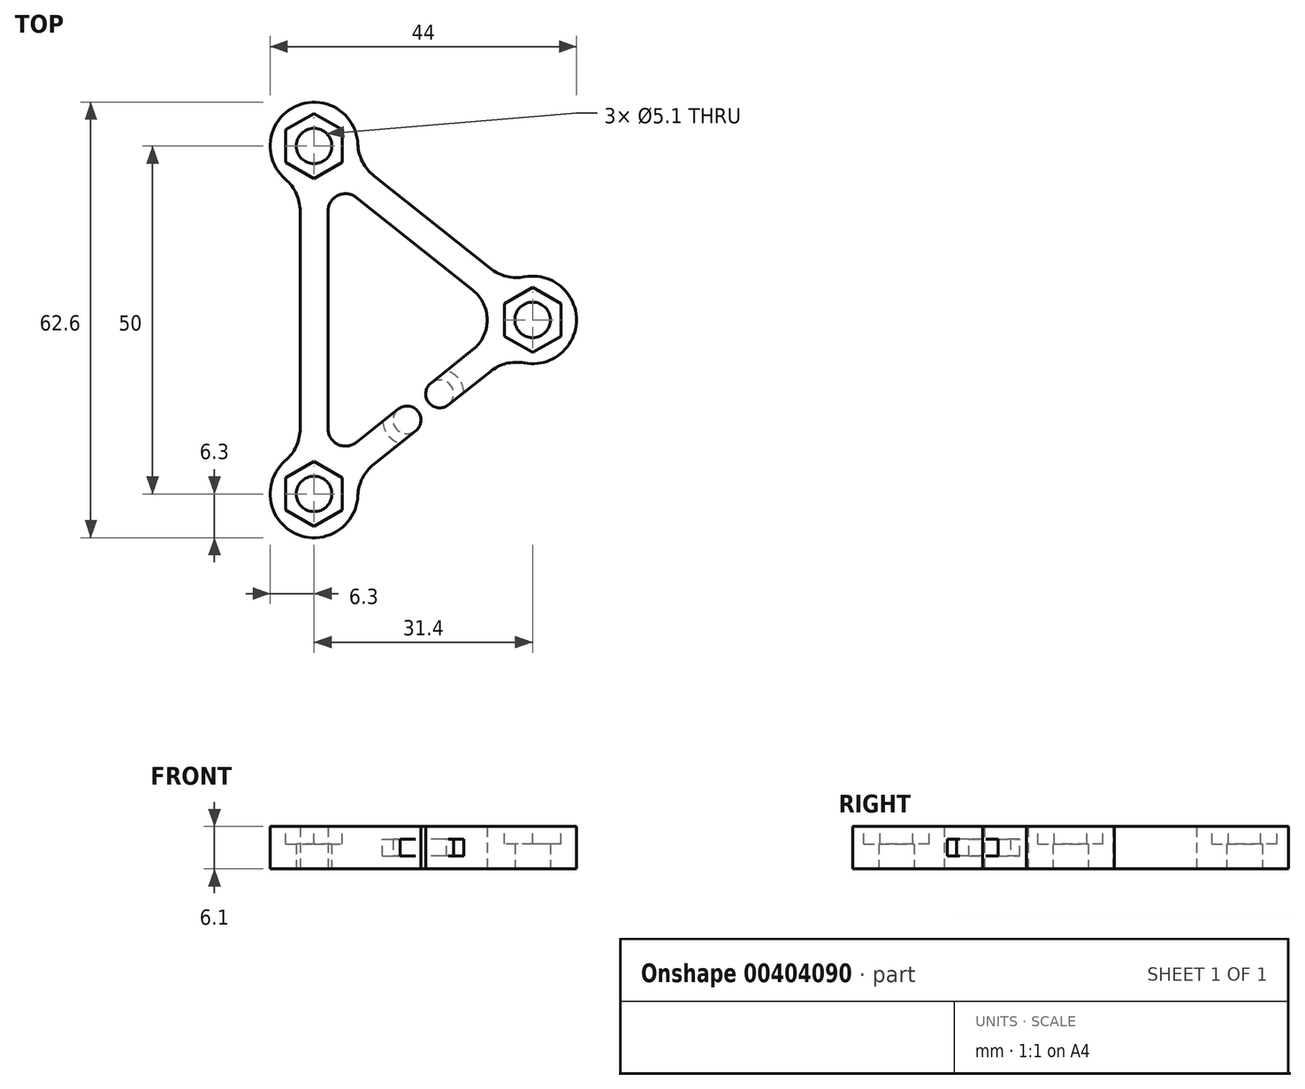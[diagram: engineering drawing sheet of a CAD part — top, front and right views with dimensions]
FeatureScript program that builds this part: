
annotation { "Feature Type Name" : "Feature", "Feature Type Description" : "" }
export const myFeature = defineFeature(function(context is Context, id is Id, definition is map)
    precondition{}
    {
        {
            var Q0;
            Q0=qCreatedBy(makeId("Top.planeOp"),FACE);
            var sketch = newSketch(context, id + "F0", { "sketchPlane" : qUnion([Q0])});
            skCircle(sketch, "E0", {"center": v(-31.4, 25) * mm, "radius": 2.55 * mm});
            skCircle(sketch, "E1", {"center": v(-31.4, -25) * mm, "radius": 2.55 * mm});
            skCircle(sketch, "E2", {"center": v(0, 0) * mm, "radius": 2.55 * mm});
            skArc(sketch, "E3", {"start": v(-25.1, 25.25) * mm, "mid": v(-34.14, 30.68) * mm, "end": v(-35.52, 20.23) * mm});
            skArc(sketch, "E4", {"start": v(-35.52, -20.23) * mm, "mid": v(-34.14, -30.68) * mm, "end": v(-25.1, -25.25) * mm});
            skArc(sketch, "E5", {"start": v(-1.17, -6.2) * mm, "mid": v(6.3, 0) * mm, "end": v(-1.17, 6.2) * mm});
            skLineSegment(sketch, "E6", {"start": v(-25.3, 17.59) * mm, "end": v(-8.6, 4.28) * mm});
            skLineSegment(sketch, "E7", {"start": v(-22.8, 20.72) * mm, "end": v(-6.1, 7.41) * mm});
            skLineSegment(sketch, "E8", {"start": v(-31.4, 25) * mm, "end": v(0, 0) * mm, "construction": true});
            skLineSegment(sketch, "E9", {"start": v(0, 0) * mm, "end": v(-31.4, -25) * mm, "construction": true});
            skLineSegment(sketch, "E10", {"start": v(-31.4, -25) * mm, "end": v(-31.4, 25) * mm, "construction": true});
            skArc(sketch, "E11", {"start": v(-25.3, 17.59) * mm, "mid": v(-27.97, 17.89) * mm, "end": v(-29.4, 15.61) * mm});
            skArc(sketch, "E12", {"start": v(-29.4, -15.61) * mm, "mid": v(-27.97, -17.89) * mm, "end": v(-25.3, -17.59) * mm});
            skArc(sketch, "E13", {"start": v(-8.6, -4.28) * mm, "mid": v(-6.53, 0) * mm, "end": v(-8.6, 4.28) * mm});
            skArc(sketch, "E14", {"start": v(-35.52, -20.23) * mm, "mid": v(-33.95, -18.15) * mm, "end": v(-33.4, -15.61) * mm});
            skArc(sketch, "E15", {"start": v(-22.8, -20.72) * mm, "mid": v(-24.45, -22.73) * mm, "end": v(-25.1, -25.25) * mm});
            skArc(sketch, "E16", {"start": v(-33.4, 15.61) * mm, "mid": v(-33.95, 18.15) * mm, "end": v(-35.52, 20.23) * mm});
            skArc(sketch, "E17", {"start": v(-25.1, 25.25) * mm, "mid": v(-24.45, 22.73) * mm, "end": v(-22.8, 20.72) * mm});
            skArc(sketch, "E18", {"start": v(-6.1, 7.41) * mm, "mid": v(-3.77, 6.26) * mm, "end": v(-1.17, 6.2) * mm});
            skArc(sketch, "E19", {"start": v(-1.17, -6.2) * mm, "mid": v(-3.77, -6.26) * mm, "end": v(-6.1, -7.41) * mm});
            skLineSegment(sketch, "E20", {"start": v(-25.3, 17.59) * mm, "end": v(-22.8, 20.72) * mm, "construction": true});
            skLineSegment(sketch, "E21", {"start": v(-8.6, 4.28) * mm, "end": v(-6.1, 7.41) * mm, "construction": true});
            skLineSegment(sketch, "E22", {"start": v(-8.6, -4.28) * mm, "end": v(-6.1, -7.41) * mm, "construction": true});
            skLineSegment(sketch, "E23", {"start": v(-33.4, -15.61) * mm, "end": v(-29.4, -15.61) * mm, "construction": true});
            skLineSegment(sketch, "E24", {"start": v(-22.8, -20.72) * mm, "end": v(-25.3, -17.59) * mm, "construction": true});
            skLineSegment(sketch, "E25", {"start": v(-33.4, -15.61) * mm, "end": v(-33.4, 15.61) * mm});
            skLineSegment(sketch, "E26", {"start": v(-29.4, -15.61) * mm, "end": v(-29.4, 15.61) * mm});
            skLineSegment(sketch, "E27", {"start": v(-33.4, 15.61) * mm, "end": v(-29.4, 15.61) * mm, "construction": true});
            skLineSegment(sketch, "E28", {"start": v(-25.3, -17.59) * mm, "end": v(-19.3, -12.8) * mm});
            skLineSegment(sketch, "E29", {"start": v(-14.6, -9.07) * mm, "end": v(-8.6, -4.28) * mm});
            skLineSegment(sketch, "E30", {"start": v(-22.8, -20.72) * mm, "end": v(-16.8, -15.93) * mm});
            skLineSegment(sketch, "E31", {"start": v(-6.1, -7.41) * mm, "end": v(-12.1, -12.2) * mm});
            skArc(sketch, "E32", {"start": v(-16.8, -15.93) * mm, "mid": v(-16.48, -13.12) * mm, "end": v(-19.3, -12.8) * mm});
            skArc(sketch, "E33", {"start": v(-14.6, -9.07) * mm, "mid": v(-14.92, -11.88) * mm, "end": v(-12.1, -12.2) * mm});
            skLineSegment(sketch, "E34", {"start": v(-29.4, 0) * mm, "end": v(0, 0) * mm, "construction": true});
            skSolve(sketch);
        }
        {
            var Q0;
            Q0=makeQuery(id+"F0.imprint","IMPRINT",FACE,{"disambiguationData":[TD([[makeQuery(id+"F0.imprint","IMPRINT",EDGE,{"derivedFrom":sQuery(id+"F0.wireOp",EDGE,"E0")}),-1.0]])]});
            extrude(context, id + "F1", {"entities" : qUnion([Q0]), "depth" : 6.1 * mm});
        }
        {
            var Q0;
            Q0=makeQuery(id+"F1.opExtrude","CAP_FACE",FACE,{"disambiguationData":[OSD([sQuery(id+"F0.wireOp",EDGE,"E0"),sQuery(id+"F0.wireOp",EDGE,"E1"),sQuery(id+"F0.wireOp",EDGE,"E2"),sQuery(id+"F0.wireOp",EDGE,"E3"),sQuery(id+"F0.wireOp",EDGE,"E4"),sQuery(id+"F0.wireOp",EDGE,"E5"),sQuery(id+"F0.wireOp",EDGE,"T5Vw66OG-G5OR-DHDx-KvU7-dnTMRq0o1A0g"),sQuery(id+"F0.wireOp",EDGE,"8mzCXc7P-Lu7A-tcA2-hDls-zUZMRrlwUirj"),sQuery(id+"F0.wireOp",EDGE,"n4Ubmgs8-MzYA-ilAs-um63-DOsCIZ42xYd5"),sQuery(id+"F0.wireOp",EDGE,"iCspHw3C-Pdpp-QPBW-yDHl-MGOv44Ga2VXa"),sQuery(id+"F0.wireOp",EDGE,"xnWTmErK-ZSIG-ryMW-Ekzr-RR3PqCajZfuL"),sQuery(id+"F0.wireOp",EDGE,"AKW5OVUo-PFRE-jSi0-v7oE-Iw4JobIG5vWv"),sQuery(id+"F0.wireOp",EDGE,"E6"),sQuery(id+"F0.wireOp",EDGE,"JkiSf5jC-OJZR-1wmq-AVkU-QwjWYPwXVpW3"),sQuery(id+"F0.wireOp",EDGE,"9YlTFYq7-sXvY-dmJ4-6YRE-gBgDyT6P94yA")])],"isStart":false});
            var sketch = newSketch(context, id + "F2", { "sketchPlane" : qUnion([Q0])});
            skCircle(sketch, "E35.cCircle", {"center": v(-31.4, 25) * mm, "radius": 4.05 * mm, "construction": true});
            skLineSegment(sketch, "E35.0", {"start": v(-27.35, 27.34) * mm, "end": v(-27.35, 22.66) * mm});
            skLineSegment(sketch, "E35.1", {"start": v(-27.35, 22.66) * mm, "end": v(-31.4, 20.32) * mm});
            skLineSegment(sketch, "E35.2", {"start": v(-31.4, 20.32) * mm, "end": v(-35.45, 22.66) * mm});
            skLineSegment(sketch, "E35.3", {"start": v(-35.45, 22.66) * mm, "end": v(-35.45, 27.34) * mm});
            skLineSegment(sketch, "E35.4", {"start": v(-35.45, 27.34) * mm, "end": v(-31.4, 29.68) * mm});
            skLineSegment(sketch, "E35.5", {"start": v(-31.4, 29.68) * mm, "end": v(-27.35, 27.34) * mm});
            skPoint(sketch, "E35.0.midPoint", {"position": v(-27.35, 25) * mm});
            skCircle(sketch, "E36.cCircle", {"center": v(-31.4, -25) * mm, "radius": 4.05 * mm, "construction": true});
            skLineSegment(sketch, "E36.0", {"start": v(-27.35, -22.66) * mm, "end": v(-27.35, -27.34) * mm});
            skLineSegment(sketch, "E36.1", {"start": v(-27.35, -27.34) * mm, "end": v(-31.4, -29.68) * mm});
            skLineSegment(sketch, "E36.2", {"start": v(-31.4, -29.68) * mm, "end": v(-35.45, -27.34) * mm});
            skLineSegment(sketch, "E36.3", {"start": v(-35.45, -27.34) * mm, "end": v(-35.45, -22.66) * mm});
            skLineSegment(sketch, "E36.4", {"start": v(-35.45, -22.66) * mm, "end": v(-31.4, -20.32) * mm});
            skLineSegment(sketch, "E36.5", {"start": v(-31.4, -20.32) * mm, "end": v(-27.35, -22.66) * mm});
            skPoint(sketch, "E36.0.midPoint", {"position": v(-27.35, -25) * mm});
            skCircle(sketch, "E37.cCircle", {"center": v(0, 0) * mm, "radius": 4.05 * mm, "construction": true});
            skLineSegment(sketch, "E37.0", {"start": v(-4.05, -2.34) * mm, "end": v(-4.05, 2.34) * mm});
            skLineSegment(sketch, "E37.1", {"start": v(-4.05, 2.34) * mm, "end": v(0, 4.68) * mm});
            skLineSegment(sketch, "E37.2", {"start": v(0, 4.68) * mm, "end": v(4.05, 2.34) * mm});
            skLineSegment(sketch, "E37.3", {"start": v(4.05, 2.34) * mm, "end": v(4.05, -2.34) * mm});
            skLineSegment(sketch, "E37.4", {"start": v(4.05, -2.34) * mm, "end": v(0, -4.68) * mm});
            skLineSegment(sketch, "E37.5", {"start": v(0, -4.68) * mm, "end": v(-4.05, -2.34) * mm});
            skPoint(sketch, "E37.0.midPoint", {"position": v(-4.05, 0) * mm});
            skSolve(sketch);
        }
        {
            var Q0;
            Q0=qSketchRegion(id+"F2",true);
            extrude(context, id + "F3", {"entities" : qUnion([Q0]), "operationType" : NewBodyOperationType.REMOVE, "oppositeDirection" : true, "depth" : 2.5 * mm});
        }
        {
            var Q0;
            Q0=qCreatedBy(makeId("Top.planeOp"),FACE);
            var Q1;
            Q1=makeQuery(id+"F2.imprint","IMPRINT",FACE,{"disambiguationData":[TD([[makeQuery(id+"F2.imprint","IMPRINT",EDGE,{"derivedFrom":sQuery(id+"F2.wireOp",EDGE,"E35.0")}),1.0]])]});
            cPlane(context, id + "F4", {"entities" : qUnion([Q0, Q1]), "cplaneType" : CPlaneType.MID_PLANE, "offset" : 3 * mm, "oppositeDirection" : true, "width" : 150 * mm, "height" : 150 * mm});
        }
        {
            var Q0;
            Q0=qCreatedBy(id+"F4.planeOp",FACE);
            var sketch = newSketch(context, id + "F5", { "sketchPlane" : qUnion([Q0])});
            skLineSegment(sketch, "E38", {"start": v(-16.8, -15.93) * mm, "end": v(-16.8, -15.93) * mm});
            skLineSegment(sketch, "E39", {"start": v(-19.3, -12.8) * mm, "end": v(-19.3, -12.8) * mm});
            skLineSegment(sketch, "E40", {"start": v(-12.1, -12.2) * mm, "end": v(-12.1, -12.2) * mm});
            skLineSegment(sketch, "E41", {"start": v(-14.6, -9.07) * mm, "end": v(-14.6, -9.07) * mm});
            skArc(sketch, "E42", {"start": v(-21.54, -14.6) * mm, "mid": v(-20.79, -16.55) * mm, "end": v(-19.05, -17.72) * mm});
            skArc(sketch, "E43", {"start": v(-12.1, -12.2) * mm, "mid": v(-11.79, -9.39) * mm, "end": v(-14.6, -9.07) * mm});
            skArc(sketch, "E44", {"start": v(-19.3, -12.8) * mm, "mid": v(-19.61, -15.61) * mm, "end": v(-16.8, -15.93) * mm});
            skLineSegment(sketch, "E45", {"start": v(-21.54, -14.6) * mm, "end": v(-19.3, -12.8) * mm});
            skLineSegment(sketch, "E46", {"start": v(-16.8, -15.93) * mm, "end": v(-19.05, -17.72) * mm});
            skArc(sketch, "E47", {"start": v(-9.86, -10.4) * mm, "mid": v(-10.61, -8.45) * mm, "end": v(-12.35, -7.28) * mm});
            skLineSegment(sketch, "E48", {"start": v(-12.35, -7.28) * mm, "end": v(-14.6, -9.07) * mm});
            skLineSegment(sketch, "E49", {"start": v(-12.1, -12.2) * mm, "end": v(-9.86, -10.4) * mm});
            skSolve(sketch);
        }
        {
            var Q0;
            Q0=qSketchRegion(id+"F5",true);
            extrude(context, id + "F6", {"entities" : qUnion([Q0]), "operationType" : NewBodyOperationType.REMOVE, "endBound" : BoundingType.SYMMETRIC, "oppositeDirection" : true, "depth" : 2.4 * mm});
        }
    });
